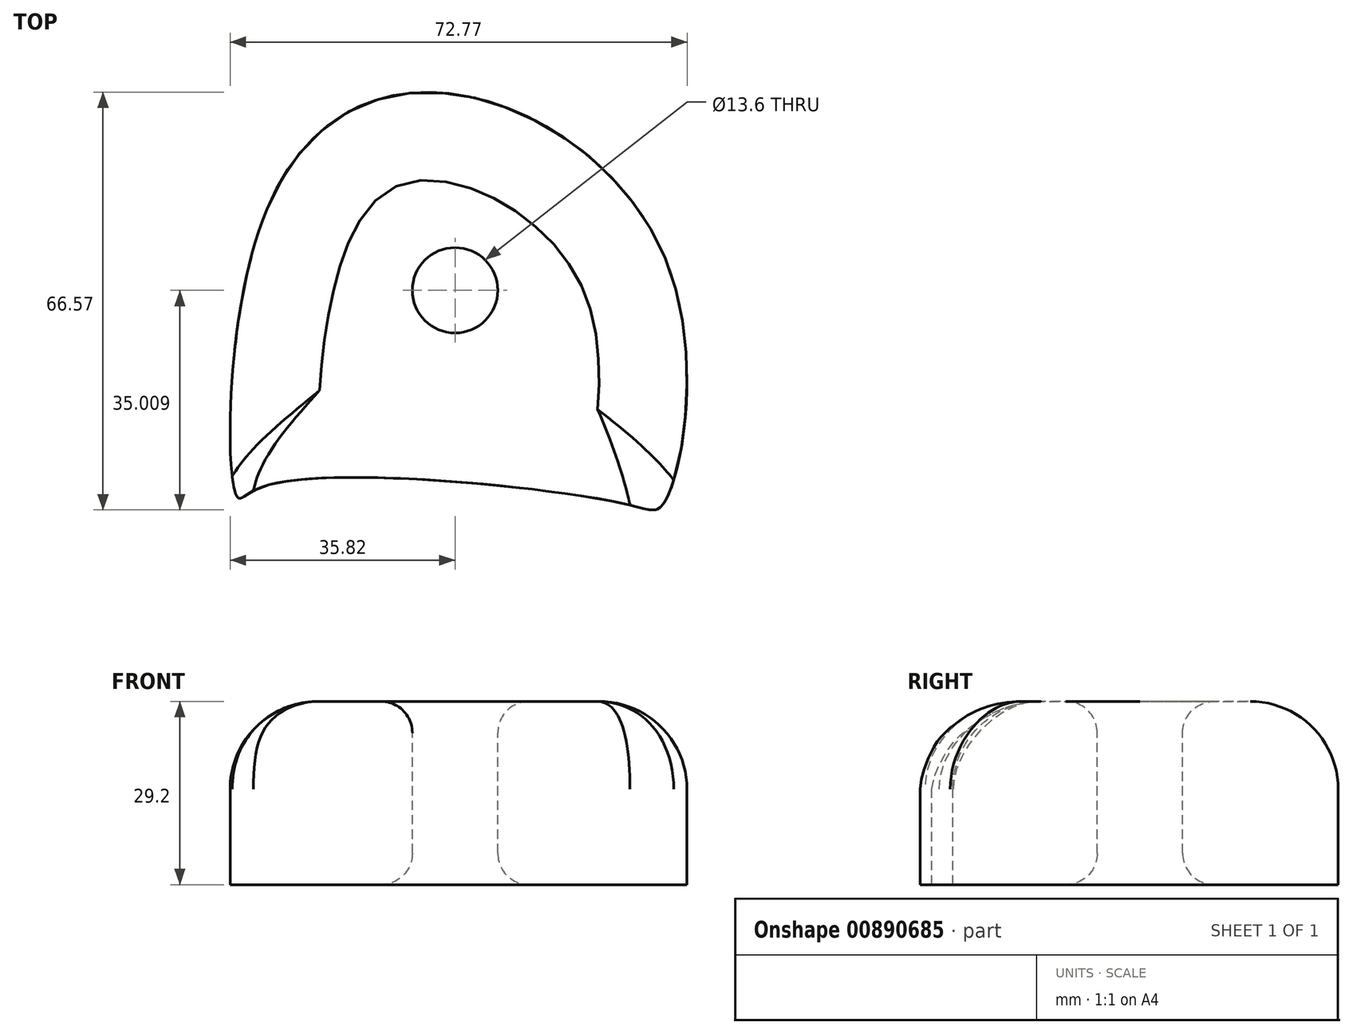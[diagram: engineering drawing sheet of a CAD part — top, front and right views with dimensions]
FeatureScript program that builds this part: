
annotation { "Feature Type Name" : "Feature", "Feature Type Description" : "" }
export const myFeature = defineFeature(function(context is Context, id is Id, definition is map)
    precondition{}
    {
        {
            var Q0;
            Q0=qCreatedBy(makeId("Top.planeOp"),FACE);
            var sketch = newSketch(context, id + "F0", { "sketchPlane" : qUnion([Q0])});
            skFitSpline(sketch, "E0", {"points": [v(-45.42, 35.22) * mm, v(-16.72, 53.73) * mm, v(18.86, 25.26) * mm, v(17.67, -11.74) * mm, v(11.74, -11.74) * mm, v(-45.9, -8.9) * mm, v(-50.17, -10.56) * mm, v(-45.42, 35.22) * mm]});
            skSolve(sketch);
        }
        {
            var Q0;
            Q0 = qSketchRegion(id + "F0", true);
            extrude(context, id + "F1", {"entities" : qUnion([Q0]), "depth" : 29.2 * mm, "offsetDistance" : 25 * mm});
        }
        {
            var Q0;
            Q0=makeQuery(id+"F1.opExtrude","CAP_EDGE",EDGE,{"disambiguationData":[OSD([sQuery(id+"F0.wireOp",EDGE,"E0")])],"isStart":false});
            fillet(context, id + "F2", {"entities" : qUnion([Q0]), "radius" : 14 * mm, "tangentPropagation" : true, "allowEdgeOverflow" : false});
        }
        {
            var Q0;
            Q0=makeQuery(id+"F1.opExtrude","CAP_FACE",FACE,{"disambiguationData":[OSD([sQuery(id+"F0.wireOp",EDGE,"E0")])],"isStart":false});
            var sketch = newSketch(context, id + "F3", { "sketchPlane" : qUnion([Q0])});
            skCircle(sketch, "E1", {"center": v(-15.47, 22.33) * mm, "radius": 6.8 * mm});
            skSolve(sketch);
        }
        {
            var Q0;
            Q0 = qSketchRegion(id + "F3", true);
            extrude(context, id + "F4", {"entities" : qUnion([Q0]), "operationType" : NewBodyOperationType.REMOVE, "oppositeDirection" : true, "depth" : 61.1 * mm, "offsetDistance" : 25 * mm});
        }
        {
            var Q0;
            Q0=makeQuery(id+"F4.boolean.opBoolean","COPY",FACE,{"derivedFrom":makeQuery(id+"F4.opExtrude","SWEPT_FACE",FACE,{"disambiguationData":[OSD([sQuery(id+"F3.wireOp",EDGE,"E1")])]})});
            fillet(context, id + "F5", {"entities" : qUnion([Q0]), "radius" : 5 * mm, "tangentPropagation" : true, "allowEdgeOverflow" : false});
        }
    });
